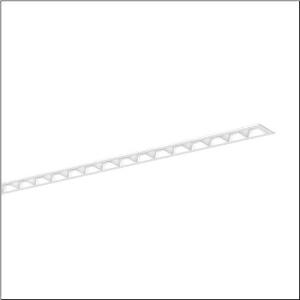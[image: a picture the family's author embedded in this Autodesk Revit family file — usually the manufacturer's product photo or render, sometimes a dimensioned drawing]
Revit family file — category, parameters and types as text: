
# Revit family: silica_r__21_51mx16db35wb_6bb0
name_source: partatom
category: Lighting Fixtures
units: mm (PartAtom-declared; Revit-internal decimal feet)

## family parameters
Cut with Voids When Loaded = No
Host = Face
Light Source = No
Part Type = Normal
Room Calculation Point = No
Round Connector Dimension = Use Diameter
Shared = No

## types (1)
- --- (1 x LED, 5400 lm, 31.4 W, 3000K)
    Apparent Load = 31 VA
    CIE Flux Codes = 83 98 100 100 100
    Color Rendering = 80
    Color Temperature = 3000K
    Default Elevation = 1800 mm
    Description = Silica® 21, office luminaire, primary light control with darklight reflector, of PMMA, white, CAT 2 (L<= 3000cd/m²), light emission: direct distribution, primary light characteristic: symmetric, installation type: recessed, LED, rated luminous flux: 5.400lm, luminous efficacy: 172lm/W, light colour: 830, colour temperature: 3000K, with terminal, 3+2-pole, max. 2.5mm², mains connection: 220..240V, AC, 50/60Hz, rated input power: 31.4W, luminaire housing, of aluminium, traffic white (RAL 9016), length: 1.528mm, width: 79mm, height: 53mm, protection rating (complete): IP20, insulation class (complete): insulation class I (protective earthing), certification: CE, permissible operating ambient temperature: 0..+35°C, standard: EN 50419, packaging unit: 1 piece
    Height = 0 mm  [stored 0 ft]
    Lamp = 1 x LED
    Lamp Light Flux = 5400 lm
    Lamp Power = 31.4 W
    Lamp count = 1
    Length = 1527 mm
    Luminous efficacy = 172 lm/W
    Manufacturer = Siteco
    ModVariant = No
    Model = 51MX16DB35WB
    Mounting Place = Ceiling
    Mounting Type = Recessed
    Number of Poles = 1
    OnlyDefault = Yes
    Power Factor = 1
    Product Name = Silica® 21
    Product group = office luminaire | ceiling recessed
    ProductGroupID = 401
    Protection Class = Protection class I
    Protection Degree = IP 20
    RLX_Detail_Level = 1
    RLX_Emergency_Light_Flux = 0 lm
    RLX_Emergency_Type = 0
    RLX_Emergency_Type_DB = No
    RlxData = <blob elided: 39449 chars, md5=b1a2ffbc>
    Socket = socket
    Standby Power = 0 W
    System Light Flux = 5400 lm
    System Power = 31 W
    Type Comments = factory setting: luminous flux: 100 % | dim-lin: 254 | 360 mA
    Type Image = l_1297786.jpg
    URL = http://relux.com
    VarID = @adj_055115
    Voltage = 0 V
    Weight = 0.00 kg
    Width = 79 mm

note: [stored X ft] marks values corroborated as IEEE doubles in the binary element streams (Revit-internal decimal feet)

## geometry (parser evidence)
native form markers: Blend x4, Sweep x10
no freeform markers — native parametric forms only
